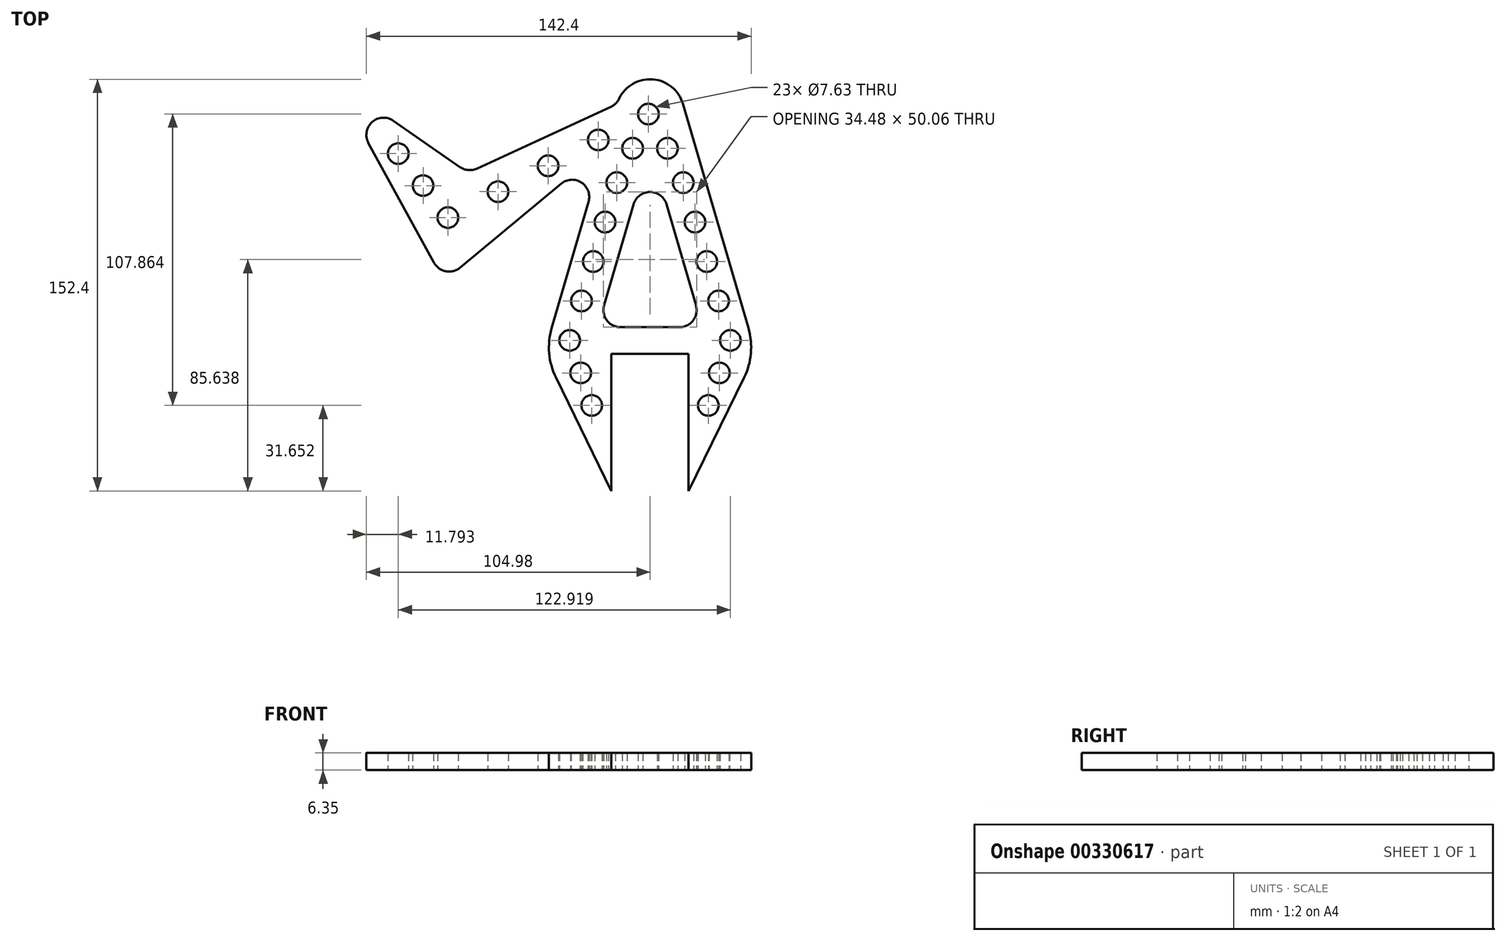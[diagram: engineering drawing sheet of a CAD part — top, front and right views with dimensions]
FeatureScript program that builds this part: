
annotation { "Feature Type Name" : "Feature", "Feature Type Description" : "" }
export const myFeature = defineFeature(function(context is Context, id is Id, definition is map)
    precondition{}
    {
        {
            var Q0;
            Q0=qCreatedBy(makeId("Top.planeOp"),FACE);
            var sketch = newSketch(context, id + "F0", { "sketchPlane" : qUnion([Q0])});
            skLineSegment(sketch, "E0", {"start": v(0, 101.6) * mm, "end": v(0, 76.2) * mm, "construction": true});
            skLineSegment(sketch, "E1.0", {"start": v(14.29, 0) * mm, "end": v(14.29, -50.8) * mm});
            skLineSegment(sketch, "E2.MirrorCS", {"start": v(-14.29, 0) * mm, "end": v(-14.29, -50.8) * mm});
            skLineSegment(sketch, "E3", {"start": v(43.67, 0) * mm, "end": v(-39.16, 0) * mm, "construction": true});
            skPoint(sketch, "E4.orphan", {"position": v(-14.29, -35.82) * mm});
            skPoint(sketch, "E5.orphan", {"position": v(14.29, -35.82) * mm});
            skLineSegment(sketch, "E6.0", {"start": v(43.67, 101.6) * mm, "end": v(-39.16, 101.6) * mm, "construction": true});
            skLineSegment(sketch, "E7.0", {"start": v(43.67, 76.2) * mm, "end": v(9.5, 76.2) * mm});
            skLineSegment(sketch, "E8", {"start": v(0, 76.2) * mm, "end": v(0, -35.82) * mm, "construction": true});
            skPoint(sketch, "E9.orphan", {"position": v(-14.29, 44.24) * mm});
            skPoint(sketch, "E10.orphan", {"position": v(14.29, 44.24) * mm});
            skLineSegment(sketch, "E11", {"start": v(-14.29, 0) * mm, "end": v(14.29, 0) * mm});
            skLineSegment(sketch, "E12", {"start": v(0, 0) * mm, "end": v(0, 76.2) * mm});
            skLineSegment(sketch, "E13.trimOffspring", {"start": v(-9.5, 76.2) * mm, "end": v(-39.16, 76.2) * mm});
            skLineSegment(sketch, "E14", {"start": v(-14.29, -50.8) * mm, "end": v(-34.83, -8.84) * mm});
            skLineSegment(sketch, "E15", {"start": v(-36.4, 9.44) * mm, "end": v(-22.74, 56.27) * mm});
            skLineSegment(sketch, "E16.MirrorCS", {"start": v(36.4, 9.44) * mm, "end": v(12.2, 92.46) * mm});
            skLineSegment(sketch, "E17.MirrorCS", {"start": v(14.29, -50.8) * mm, "end": v(34.83, -8.84) * mm});
            skPoint(sketch, "E18.orphan", {"position": v(-12.2, 92.46) * mm});
            skLineSegment(sketch, "E19", {"start": v(-6.1, 55.3) * mm, "end": v(-17, 17.94) * mm});
            skLineSegment(sketch, "E20", {"start": v(-10.9, 9.8) * mm, "end": v(0, 9.8) * mm});
            skLineSegment(sketch, "E21.MirrorCS", {"start": v(10.9, 9.8) * mm, "end": v(0, 9.8) * mm});
            skLineSegment(sketch, "E22.MirrorCS", {"start": v(6.1, 55.3) * mm, "end": v(17, 17.94) * mm});
            skLineSegment(sketch, "E23", {"start": v(-32.9, 62.94) * mm, "end": v(-70.32, 31.85) * mm});
            skLineSegment(sketch, "E24", {"start": v(-79.95, 33.68) * mm, "end": v(-104.2, 77.98) * mm});
            skLineSegment(sketch, "E25", {"start": v(-95, 86.24) * mm, "end": v(-70.3, 69.09) * mm});
            skLineSegment(sketch, "E26", {"start": v(-64.01, 68.54) * mm, "end": v(-14.5, 91.39) * mm});
            skArc(sketch, "E27", {"start": v(12.2, 92.46) * mm, "mid": v(1.04, 101.56) * mm, "end": v(-11.45, 94.4) * mm});
            skPoint(sketch, "E28.visualSharp", {"position": v(-67.3, 67.02) * mm});
            skArc(sketch, "E28.filletArc", {"start": v(-70.3, 69.09) * mm, "mid": v(-67.23, 67.98) * mm, "end": v(-64.01, 68.54) * mm});
            skPoint(sketch, "E29.visualSharp", {"position": v(-76.25, 26.92) * mm});
            skArc(sketch, "E29.filletArc", {"start": v(-79.95, 33.68) * mm, "mid": v(-75.57, 30.5) * mm, "end": v(-70.32, 31.85) * mm});
            skArc(sketch, "E30.filletArc", {"start": v(-95, 86.24) * mm, "mid": v(-102.87, 85.75) * mm, "end": v(-104.2, 77.98) * mm});
            skArc(sketch, "E31.filletArc", {"start": v(-14.5, 91.39) * mm, "mid": v(-12.72, 92.63) * mm, "end": v(-11.45, 94.4) * mm});
            skPoint(sketch, "E32.visualSharp", {"position": v(-39.16, 0) * mm});
            skArc(sketch, "E32.filletArc", {"start": v(-36.4, 9.44) * mm, "mid": v(-37.32, 0.16) * mm, "end": v(-34.83, -8.84) * mm});
            skPoint(sketch, "E33.visualSharp", {"position": v(39.16, 0) * mm});
            skArc(sketch, "E33.filletArc", {"start": v(34.83, -8.84) * mm, "mid": v(37.32, 0.16) * mm, "end": v(36.4, 9.44) * mm});
            skPoint(sketch, "E34.visualSharp", {"position": v(-19.36, 9.8) * mm});
            skArc(sketch, "E34.filletArc", {"start": v(-17, 17.94) * mm, "mid": v(-15.98, 12.35) * mm, "end": v(-10.9, 9.8) * mm});
            skPoint(sketch, "E35.visualSharp", {"position": v(19.36, 9.8) * mm});
            skArc(sketch, "E35.filletArc", {"start": v(10.9, 9.8) * mm, "mid": v(15.98, 12.35) * mm, "end": v(17, 17.94) * mm});
            skPoint(sketch, "E36.visualSharp", {"position": v(0, 76.2) * mm});
            skArc(sketch, "E36.filletArc", {"start": v(6.1, 55.3) * mm, "mid": v(0, 59.87) * mm, "end": v(-6.1, 55.3) * mm});
            skPoint(sketch, "E37.visualSharp", {"position": v(-16.93, 76.2) * mm});
            skArc(sketch, "E37.filletArc", {"start": v(-22.74, 56.27) * mm, "mid": v(-25.36, 63.36) * mm, "end": v(-32.9, 62.94) * mm});
            skLineSegment(sketch, "E38", {"start": v(-98.63, 81.03) * mm, "end": v(-74.78, 50.58) * mm, "construction": true});
            skLineSegment(sketch, "E39", {"start": v(-74.78, 50.58) * mm, "end": v(0, 88.9) * mm, "construction": true});
            skLineSegment(sketch, "E40", {"start": v(0, 88.9) * mm, "end": v(-11.9, 63.1) * mm, "construction": true});
            skLineSegment(sketch, "E41", {"start": v(-11.9, 63.1) * mm, "end": v(-29.27, 4.37) * mm, "construction": true});
            skLineSegment(sketch, "E42", {"start": v(-29.27, 4.37) * mm, "end": v(-23.01, -10.05) * mm, "construction": true});
            skLineSegment(sketch, "E43.MirrorCS", {"start": v(29.27, 4.37) * mm, "end": v(23.01, -10.05) * mm, "construction": true});
            skLineSegment(sketch, "E44.MirrorCS", {"start": v(11.9, 63.1) * mm, "end": v(29.27, 4.37) * mm, "construction": true});
            skLineSegment(sketch, "E45.MirrorCS", {"start": v(0, 88.9) * mm, "end": v(11.9, 63.1) * mm, "construction": true});
            skCircle(sketch, "E46", {"center": v(-93.19, 74.08) * mm, "radius": 3.82 * mm});
            skCircle(sketch, "E47.1.0.0", {"center": v(-84, 62.24) * mm, "radius": 3.82 * mm});
            skCircle(sketch, "E47.2.0.0", {"center": v(-74.82, 50.4) * mm, "radius": 3.82 * mm});
            skLineSegment(sketch, "E47.direction1", {"start": v(-93.19, 74.08) * mm, "end": v(-84, 62.24) * mm, "construction": true});
            skCircle(sketch, "E48.1.0.0", {"center": v(-56.26, 59.98) * mm, "radius": 3.82 * mm});
            skCircle(sketch, "E48.2.0.0", {"center": v(-37.71, 69.56) * mm, "radius": 3.82 * mm});
            skCircle(sketch, "E48.3.0.0", {"center": v(-19.16, 79.14) * mm, "radius": 3.82 * mm});
            skCircle(sketch, "E48.4.0.0", {"center": v(-0.6, 88.72) * mm, "radius": 3.82 * mm});
            skLineSegment(sketch, "E48.direction1", {"start": v(-74.82, 50.4) * mm, "end": v(-56.26, 59.98) * mm, "construction": true});
            skCircle(sketch, "E49.1.0.0", {"center": v(-6.45, 76.03) * mm, "radius": 3.82 * mm});
            skCircle(sketch, "E49.2.0.0", {"center": v(-12.29, 63.33) * mm, "radius": 3.82 * mm});
            skLineSegment(sketch, "E49.direction1", {"start": v(-0.6, 88.72) * mm, "end": v(-6.45, 76.03) * mm, "construction": true});
            skCircle(sketch, "E50.1.0.0", {"center": v(-16.65, 48.73) * mm, "radius": 3.82 * mm});
            skCircle(sketch, "E50.2.0.0", {"center": v(-21.01, 34.13) * mm, "radius": 3.82 * mm});
            skCircle(sketch, "E50.3.0.0", {"center": v(-25.37, 19.53) * mm, "radius": 3.82 * mm});
            skCircle(sketch, "E50.4.0.0", {"center": v(-29.73, 4.92) * mm, "radius": 3.82 * mm});
            skLineSegment(sketch, "E50.direction1", {"start": v(-12.29, 63.33) * mm, "end": v(-16.65, 48.73) * mm, "construction": true});
            skCircle(sketch, "E51.1.0.0", {"center": v(-25.65, -7.11) * mm, "radius": 3.82 * mm});
            skCircle(sketch, "E51.2.0.0", {"center": v(-21.58, -19.15) * mm, "radius": 3.82 * mm});
            skLineSegment(sketch, "E51.direction1", {"start": v(-29.73, 4.92) * mm, "end": v(-25.65, -7.11) * mm, "construction": true});
            skCircle(sketch, "E52.MirrorC", {"center": v(21.58, -19.15) * mm, "radius": 3.82 * mm});
            skCircle(sketch, "E53.MirrorC", {"center": v(25.65, -7.11) * mm, "radius": 3.82 * mm});
            skCircle(sketch, "E54.MirrorC", {"center": v(29.73, 4.92) * mm, "radius": 3.82 * mm});
            skCircle(sketch, "E55.MirrorC", {"center": v(25.37, 19.53) * mm, "radius": 3.82 * mm});
            skCircle(sketch, "E56.MirrorC", {"center": v(21.01, 34.13) * mm, "radius": 3.82 * mm});
            skCircle(sketch, "E57.MirrorC", {"center": v(16.65, 48.73) * mm, "radius": 3.82 * mm});
            skCircle(sketch, "E58.MirrorC", {"center": v(12.29, 63.33) * mm, "radius": 3.82 * mm});
            skCircle(sketch, "E59.MirrorC", {"center": v(6.45, 76.03) * mm, "radius": 3.82 * mm});
            skSolve(sketch);
        }
        {
            var Q0;
            {var subQ3=sQuery(id+"F0.wireOp",EDGE,"E1.0");Q0=makeQuery(id+"F0.imprint","IMPRINT",FACE,{"disambiguationData":[TD([[makeQuery(id+"F0.imprint","IMPRINT",EDGE,{"derivedFrom":subQ3}),1.0]])]});}
            extrude(context, id + "F1", {"entities" : qUnion([Q0]), "depth" : 6.35 * mm, "offsetDistance" : 25.4 * mm});
        }
    });
